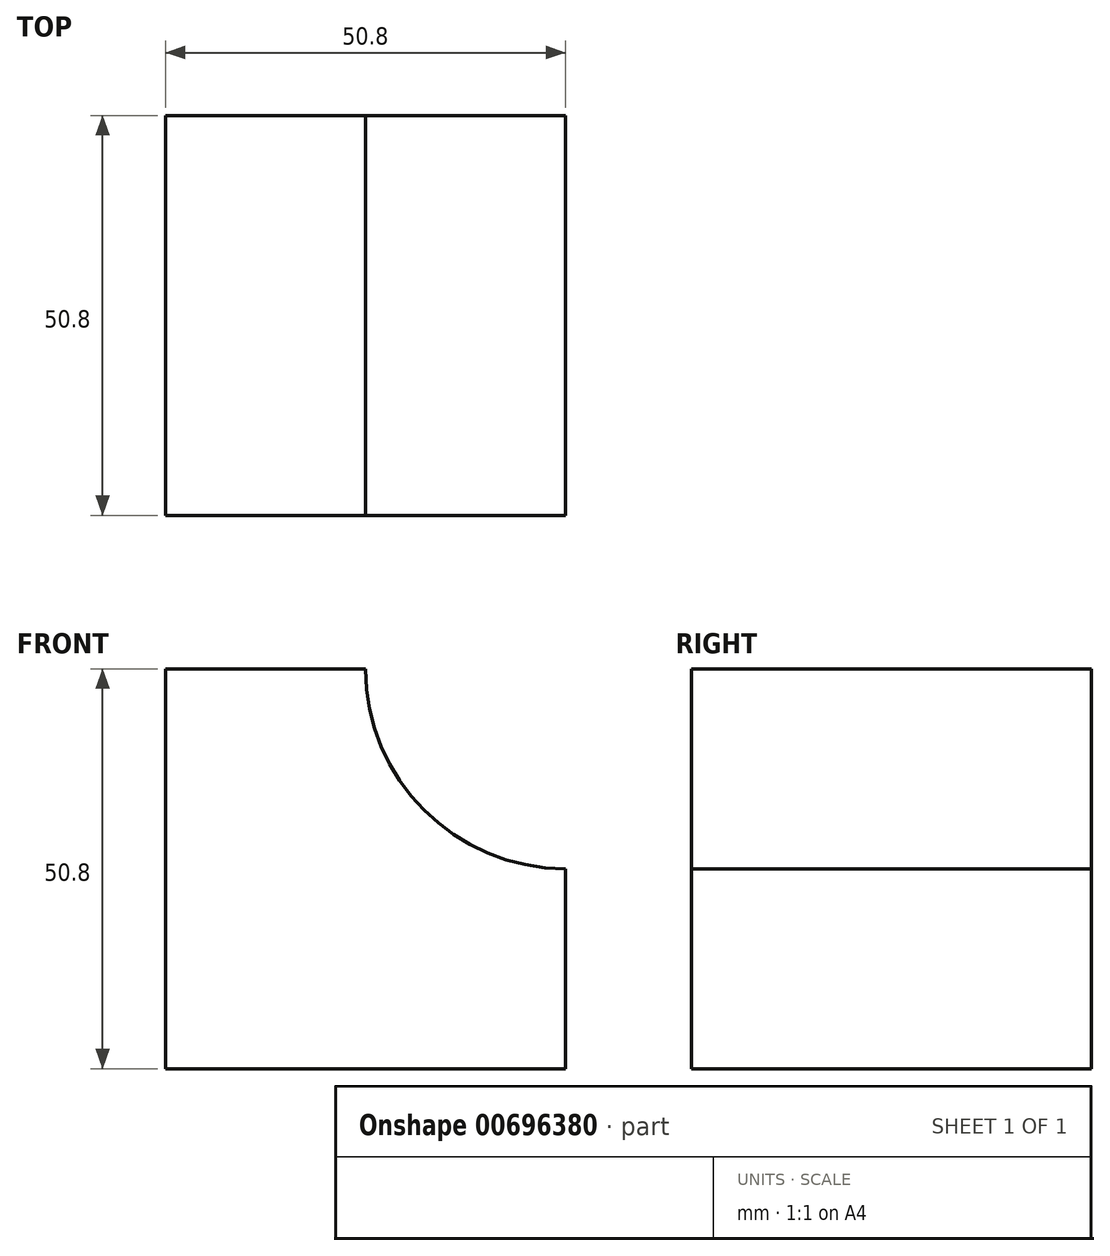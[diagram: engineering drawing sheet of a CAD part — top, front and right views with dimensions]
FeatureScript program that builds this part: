
annotation { "Feature Type Name" : "Feature", "Feature Type Description" : "" }
export const myFeature = defineFeature(function(context is Context, id is Id, definition is map)
    precondition{}
    {
        {
            var Q0;
            Q0=qCreatedBy(makeId("Front.planeOp"),FACE);
            var sketch = newSketch(context, id + "F0", { "sketchPlane" : qUnion([Q0])});
            skLineSegment(sketch, "E0.bottom", {"start": v(0, 0) * mm, "end": v(-50.8, 0) * mm});
            skLineSegment(sketch, "E0.top", {"start": v(-25.4, 50.8) * mm, "end": v(-50.8, 50.8) * mm});
            skLineSegment(sketch, "E0.left", {"start": v(0, 0) * mm, "end": v(0, 25.4) * mm});
            skLineSegment(sketch, "E0.right", {"start": v(-50.8, 0) * mm, "end": v(-50.8, 50.8) * mm});
            skArc(sketch, "E1", {"start": v(-25.4, 50.8) * mm, "mid": v(-17.96, 32.84) * mm, "end": v(0, 25.4) * mm});
            skSolve(sketch);
        }
        {
            var Q0;
            Q0 = qSketchRegion(id + "F0", true);
            extrude(context, id + "F1", {"entities" : qUnion([Q0]), "depth" : 50.8 * mm, "offsetDistance" : 25.4 * mm});
        }
    });
